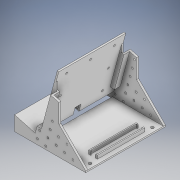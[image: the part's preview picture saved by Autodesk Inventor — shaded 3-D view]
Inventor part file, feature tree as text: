
AUTODESK INVENTOR PART (.ipt)
format: ipt  version: 2022 (Build 260153000, 153)  size: 387,072 bytes
history: native  units: in
note: dims shown in document units (in); Inventor stores cm internally (conversion verified against a paired STEP export)
features: extrude x14, sketch x11, projected_geometry x2, plane x1, chamfer x1
ambient origin geometry x8: Origin, YZ Plane, XZ Plane, XY Plane, X Axis, Y Axis, Z Axis, Center Point
bodies: Solid1 (feature_tree)
feature tree (29):
  sketch  "Sketch1"  dims[d4=1.0in d8=0.1in]
  extrude  "Extrusion1"  Depth=0.1in
  plane  "Work Plane1"
  extrude  "Extrusion2"  TaperAngle=105.0deg  [1 undecoded]
  extrude  "Extrusion3"  Depth=0.1in
  sketch  "Sketch6"  dims[d21=0.1339in d22=0.5906in]
  extrude  "Extrusion5"  Depth=0.5906in
  extrude  "Extrusion6"  Depth=0.5906in
  chamfer  "Chamfer1"  Distance=0.5906in
  extrude  "Extrusion7"  Depth=0.1in
  extrude  "Extrusion8"  Depth=0.1in
  extrude  "Extrusion9"  Depth=0.1in
  sketch  "Sketch10"  dims[d27=0.1339in]
  extrude  "Extrusion11"  Depth=0.1in
  extrude  "Extrusion12"  Depth=0.1in
  sketch  "Sketch11"  dims[d28=0.5906in]
  extrude  "Extrusion13"  Depth=0.1in
  extrude  "Extrusion14"  Depth=0.1in
  extrude  "Extrusion15"  Depth=0.1in
  extrude  "Extrusion16"  Depth=0.1in
  sketch  "Sketch3"  dims[d11=0.0039in d12=105.0deg]
  projected_geometry  "Projected Loop1"
  sketch  "Sketch4"  dims[d16=0.1in d20=0.5906in]
  sketch  "Sketch7"  dims[d23=0.1339in d24=0.5906in]
  sketch  "Sketch8"  dims[d25=0.1339in]
  sketch  "Sketch9"  dims[d26=0.5906in]
  sketch  "Sketch12"  dims[d29=0.1339in]
  sketch  "Sketch13"  dims[d30=0.5906in d32=0.5906in d33=0.5906in d34=0.5906in d35=0.5906in d36=0.5906in d37=0.5906in d38=0.5906in d39=0.5906in d40=0.1339in d41=0.1339in d42=0.1339in d43=0.1339in d44=0.1339in d45=0.1339in d46=0.1339in d47=0.1339in d48=0.1339in d49=5.4665in d50=0.0in d51=2.7333in d53=0.1181in d54=0.1in d56=5.1909in d57=0.0in d58=0.3937in d59=0.3937in d60=0.1181in d61=0.0in d62=0.0in d74=0.4528in d75=3.1047in d76=0.0787in d77=0.2362in d78=0.0in d79=0.2362in d80=0.0in d81=0.0394in d82=0.0787in d83=45.0deg d84=0.4818in d85=1.6434in d86=1.6434in d89=2.0826in d90=3.6914in d91=0.1398in d92=0.3309in d93=0.0in d94=0.1969in d95=0.3309in d96=0.0in d98=0.1339in d99=0.1339in d101=165.0deg d102=90.0deg d103=0.3937in d104=0.0in d111=75.0deg d112=0.1in d113=0.4331in d114=0.0in d115=0.5331in d116=0.0in d117=0.4331in d118=0.0in d119=0.5331in d120=0.0in d121=0.1in d122=0.0in d123=0.1in d124=0.0in]
  projected_geometry  "Projected Loop2"
note: 1 required parameter value undecoded (feature->parameter linkage not recoverable at this tier; creation-order binding heuristic only, values carry confidence <= 0.55)
